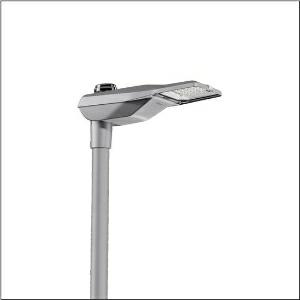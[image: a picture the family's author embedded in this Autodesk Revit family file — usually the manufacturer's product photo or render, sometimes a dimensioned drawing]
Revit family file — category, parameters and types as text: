
# Revit family: streetlight_sl_21_micro___p0_8a_5xe5u47n08cb_fda4
name_source: partatom
category: Lighting Fixtures
units: mm (PartAtom-declared; Revit-internal decimal feet)

## family parameters
Cut with Voids When Loaded = No
Host = Face
Light Source = No
Part Type = Normal
Room Calculation Point = No
Round Connector Dimension = Use Diameter
Shared = No

## types (1)
- --- (1 x LED, 2340 lm, 15.8 W, 4000K)
    Apparent Load = 16 VA
    CIE Flux Codes = 33 69 96 100 100
    Color Rendering = 70
    Color Temperature = 4000K
    Default Elevation = 1800 mm
    Description = Streetlight SL 21 micro, mast luminaire, primary light control with lens, of PMMA, primary optical cover: cover, of toughened safety glass, transparent, light distribution: P0.8a, light emission: direct distribution, primary light characteristic: asymmetric, installation type: post-top, LED, 3G 1.5mm², High Power LED, rated luminous flux: 2.340lm, luminous efficacy: 148lm/W, light colour: 740, colour temperature: 4000K, control gear: NEMA (7pin), control: flexible luminous flux parameterisation, time-dependent luminous flux control, constant luminous flux control, pre-setting: linear dimming characteristic, overheat protection, mains connection: 230..240V, AC, 50/60Hz, connection cable pre-assembled, cable length: 6,5m, wiring characteristics: H07RN-F, start of lifetime: 16W, end of service life: 16W, reduction: 8W, luminaire housing, of diecast aluminium (EN AC-44300), powder-coated, Siteco® metallic grey (DB 702S), corrosivity category C5 mid according to DIN EN ISO 12944, multi-level sealing system, sealing non-destructively replaceable, inclination adjustable: 0°, 5°, 10°, 15°, length: 528mm, width: 235mm, height: 110mm, spigot size: 76/60mm (post-top), mounting height: 4..8m, protection rating (complete): IP66, insulation class (complete): insulation class I (protective earthing), certification: CE, ENEC, ENEC+, VDE, impact resistance: IK09, permissible operating ambient temperature for outdoor applications: -40..+50°C, standard-compliant lighting for roads and squares, packaging unit: 1 piece

Light Distribution: P0.8a
    Height = 110 mm
    Lamp = 1 x LED
    Lamp Light Flux = 2340 lm
    Lamp Power = 15.8 W
    Lamp count = 1
    Length = 528 mm
    Luminous efficacy = 148 lm/W
    Manufacturer = Siteco
    ModVariant = No
    Model = 5XE5U47N08CB
    Number of Poles = 1
    OnlyDefault = Yes
    Power Factor = 1
    Product Name = Streetlight SL 21 micro | P0.8a
    Product group = mast luminaire | pylon top
    ProductGroupID = 6100
    Protection Class = Protection class I
    Protection Degree = IP 66
    RLX_Detail_Level = 1
    RLX_Emergency_Light_Flux = 0 lm
    RLX_Emergency_Type = 0
    RLX_Emergency_Type_DB = No
    RlxData = <blob elided: 98173 chars, md5=97e283bf>
    Socket = socket
    Standby Power = 0 W
    System Light Flux = 2340 lm
    System Power = 16 W
    Type Comments = factory setting: luminous flux: 100 % | dim-lin: 254 | 300 mA
    Type Image = l_1294375.jpg
    URL = http://relux.com
    VarID = @adj_070812
    Voltage = 0 V
    Weight = 0.00 kg
    Width = 235 mm

## geometry (parser evidence)
native form markers: Blend x4, Sweep x11
no freeform markers — native parametric forms only
